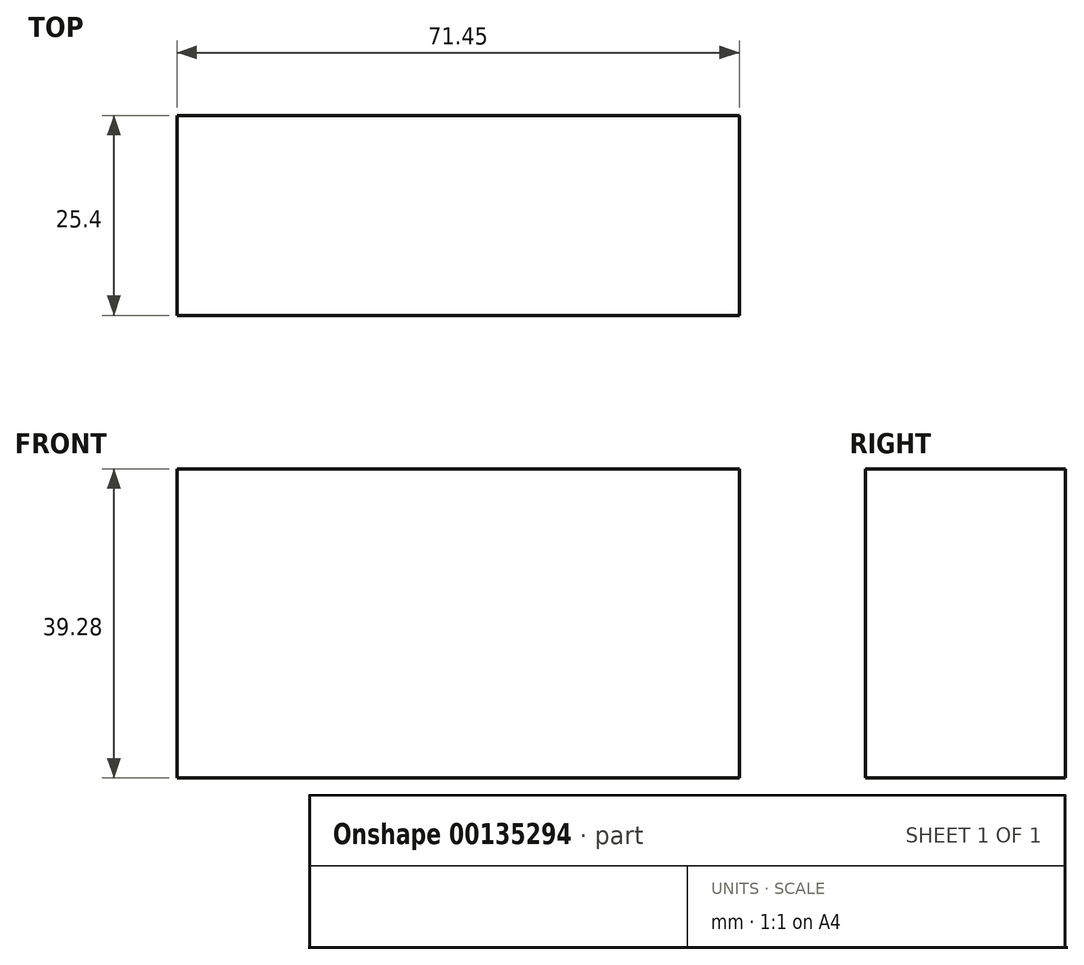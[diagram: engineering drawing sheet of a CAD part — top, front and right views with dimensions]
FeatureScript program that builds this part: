
annotation { "Feature Type Name" : "Feature", "Feature Type Description" : "" }
export const myFeature = defineFeature(function(context is Context, id is Id, definition is map)
    precondition{}
    {
        {
            var Q0;
            Q0=qCreatedBy(makeId("Front.planeOp"),FACE);
            var sketch = newSketch(context, id + "F0", { "sketchPlane" : qUnion([Q0])});
            skLineSegment(sketch, "E0.bottom", {"start": v(26.41, 19.64) * mm, "end": v(-26.41, 19.64) * mm});
            skLineSegment(sketch, "E0.top", {"start": v(26.41, -19.64) * mm, "end": v(-26.41, -19.64) * mm});
            skLineSegment(sketch, "E0.left", {"start": v(26.41, 19.64) * mm, "end": v(26.41, -19.64) * mm});
            skLineSegment(sketch, "E0.right", {"start": v(-26.41, 19.64) * mm, "end": v(-26.41, -19.64) * mm});
            skPoint(sketch, "E0.middle", {"position": v(0, 0) * mm});
            skSolve(sketch);
        }
        {
            var Q0;
            Q0=sQuery(id+"F0.wireOp",EDGE,"E0.right");
            var Q1;
            Q1=sQuery(id+"F0.wireOp",EDGE,"E0.bottom");
            var Q2;
            Q2=sQuery(id+"F0.wireOp",EDGE,"E0.top");
            var Q3;
            Q3=sQuery(id+"F0.wireOp",EDGE,"E0.left");
            extrude(context, id + "F1", {"bodyType" : ToolBodyType.SURFACE, "surfaceEntities" : qUnion([Q0, Q1, Q2, Q3]), "depth" : 25.4 * mm});
        }
        {
            var Q0;
            Q0=makeQuery(id+"F1.opExtrude","SWEPT_FACE",FACE,{"disambiguationData":[OSD([sQuery(id+"F0.wireOp",EDGE,"E0.left")])]});
            extrude(context, id + "F2", {"entities" : qUnion([Q0]), "depth" : 71.45 * mm});
        }
    });
